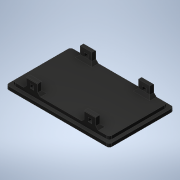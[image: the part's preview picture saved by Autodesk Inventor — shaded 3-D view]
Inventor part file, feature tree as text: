
AUTODESK INVENTOR PART (.ipt)
format: ipt  version: 2020.1 (Build 241239000, 239)  size: 206,336 bytes
history: native  units: in
note: dims shown in document units (in); Inventor stores cm internally (conversion verified against a paired STEP export)
features: fillet x8, sketch x3, extrude x2, chamfer x2, other x1
ambient origin geometry x8: Origin, YZ Plane, XZ Plane, XY Plane, X Axis, Y Axis, Z Axis, Center Point
bodies: Solid1 (feature_tree)
feature tree (16):
  extrude  "Extrusion1"  Depth=1.9685in
  extrude  "Extrusion2"  Depth=0.0984in TaperAngle=0.0deg
  fillet  "Fillet1"  Radius=0.0787in
  fillet  "Fillet2"  Radius=0.0787in
  fillet  "Fillet3"  Radius=0.0787in
  fillet  "Fillet4"  Radius=0.0787in
  fillet  "Fillet5"  Radius=0.0984in
  fillet  "Fillet6"  Radius=0.0984in
  fillet  "Fillet7"  Radius=0.0984in
  other  "Snap Fit1"
  chamfer  "Chamfer1"  Distance=0.0787in
  fillet  "Fillet8"  Radius=0.0787in
  chamfer  "Chamfer2"  Distance=0.0787in
  sketch  "Sketch2"  dims[d1=3.1496in d2=1.9685in]
  sketch  "Sketch3"  dims[d3=0.0984in d4=0.0in d5=0.0984in d6=0.0in d7=0.0787in d8=0.0787in d9=0.0787in d10=0.0787in d13=0.0984in d14=0.0984in d15=0.0984in]
  sketch  "Sketch5"  dims[d16=0.0984in d17=0.0787in d18=0.0787in d19=0.0787in d22=0.315in d23=0.1181in d24=0.1181in d25=0.3543in d26=0.1181in d27=0.1181in d28=0.1181in d29=0.1181in d30=0.0in d31=0.0in d32=0.0in d33=0.0in d34=0.5906in d35=0.5906in d36=0.5906in d37=0.5906in d38=1.5748in d39=0.9843in d40=0.0197in d41=0.0787in d42=45.0deg d50=0.0787in d51=1.7717in d52=2.9528in d53=0.0787in d54=0.0787in d55=45.0deg]
